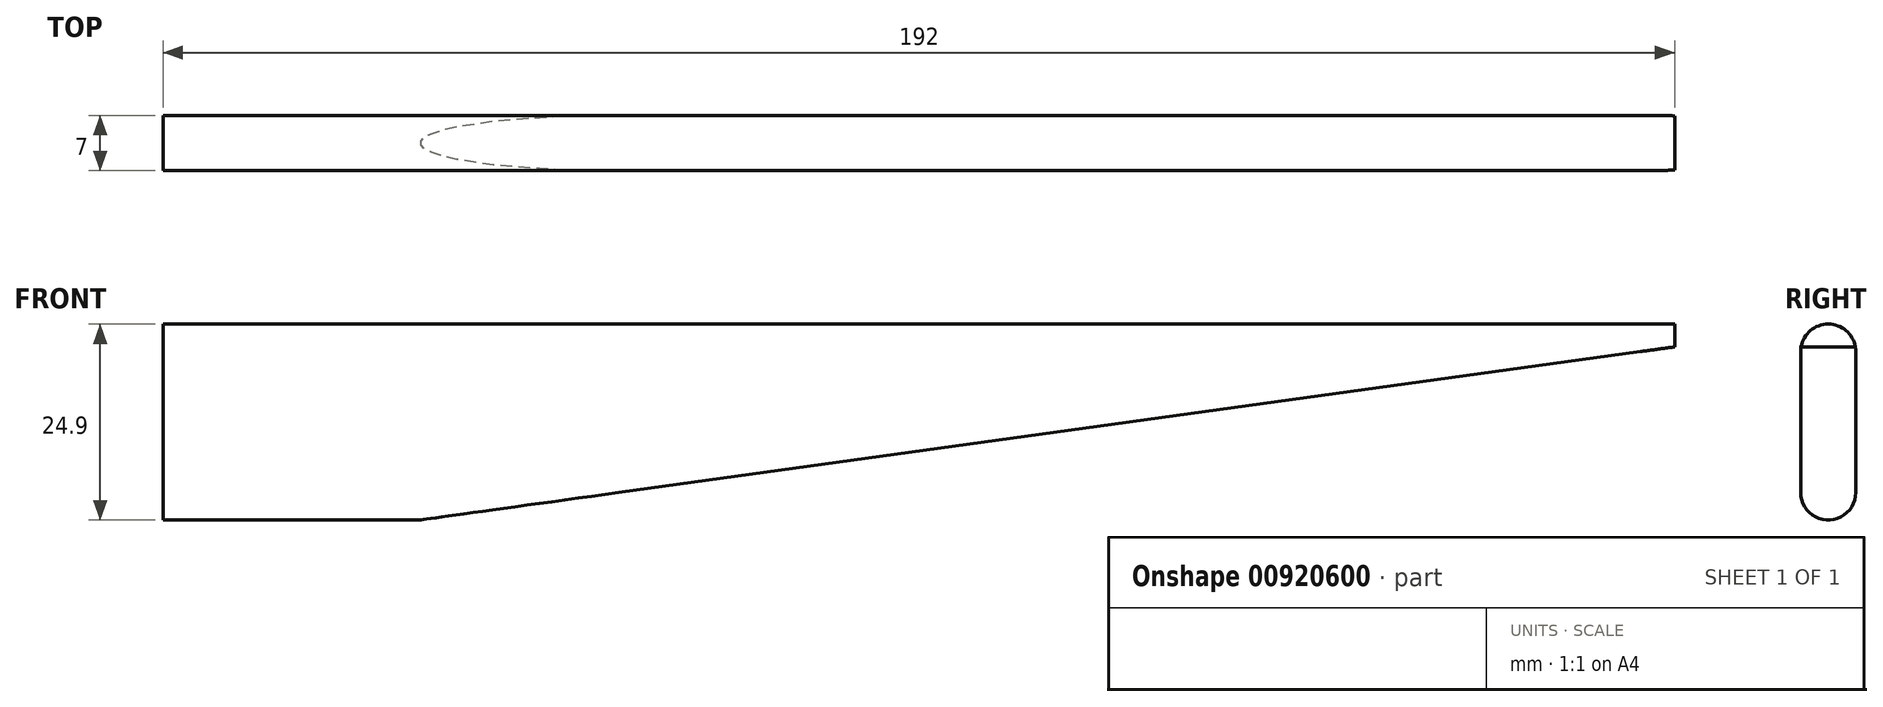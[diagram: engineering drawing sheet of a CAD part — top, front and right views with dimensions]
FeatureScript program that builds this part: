
annotation { "Feature Type Name" : "Feature", "Feature Type Description" : "" }
export const myFeature = defineFeature(function(context is Context, id is Id, definition is map)
    precondition{}
    {
        {
            var Q0;
            Q0=qCreatedBy(makeId("Front.planeOp"),FACE);
            var sketch = newSketch(context, id + "F0", { "sketchPlane" : qUnion([Q0])});
            skLineSegment(sketch, "E0", {"start": v(0, 0) * mm, "end": v(0, -24.9) * mm});
            skLineSegment(sketch, "E1", {"start": v(0, -24.9) * mm, "end": v(32.5, -24.9) * mm});
            skLineSegment(sketch, "E2", {"start": v(32.5, -24.9) * mm, "end": v(192, -2.9) * mm});
            skLineSegment(sketch, "E3", {"start": v(192, -2.9) * mm, "end": v(192, 0) * mm});
            skLineSegment(sketch, "E4", {"start": v(192, 0) * mm, "end": v(0, 0) * mm});
            skSolve(sketch);
        }
        {
            var Q0;
            Q0=makeQuery(id+"F0.imprint","IMPRINT",FACE,{"disambiguationData":[TD([[makeQuery(id+"F0.imprint","IMPRINT",EDGE,{"derivedFrom":sQuery(id+"F0.wireOp",EDGE,"E0")}),1.0]])]});
            extrude(context, id + "F1", {"entities" : qUnion([Q0]), "depth" : 7 * mm, "offsetDistance" : 25 * mm, "symmetric" : true});
        }
        {
            var Q0;
            Q0=makeQuery(id+"F1.opExtrude","CAP_EDGE",EDGE,{"disambiguationData":[OSD([sQuery(id+"F0.wireOp",EDGE,"E4")])],"isStart":false});
            var Q1;
            Q1=makeQuery(id+"F1.opExtrude","CAP_EDGE",EDGE,{"disambiguationData":[OSD([sQuery(id+"F0.wireOp",EDGE,"E4")])],"isStart":true});
            var Q2;
            Q2=makeQuery(id+"F1.opExtrude","CAP_EDGE",EDGE,{"disambiguationData":[OSD([sQuery(id+"F0.wireOp",EDGE,"E1")])],"isStart":false});
            var Q3;
            Q3=makeQuery(id+"F1.opExtrude","CAP_EDGE",EDGE,{"disambiguationData":[OSD([sQuery(id+"F0.wireOp",EDGE,"E1")])],"isStart":true});
            fillet(context, id + "F2", {"entities" : qUnion([Q0, Q1, Q2, Q3]), "radius" : 3.5 * mm, "tangentPropagation" : true, "allowEdgeOverflow" : false});
        }
    });
